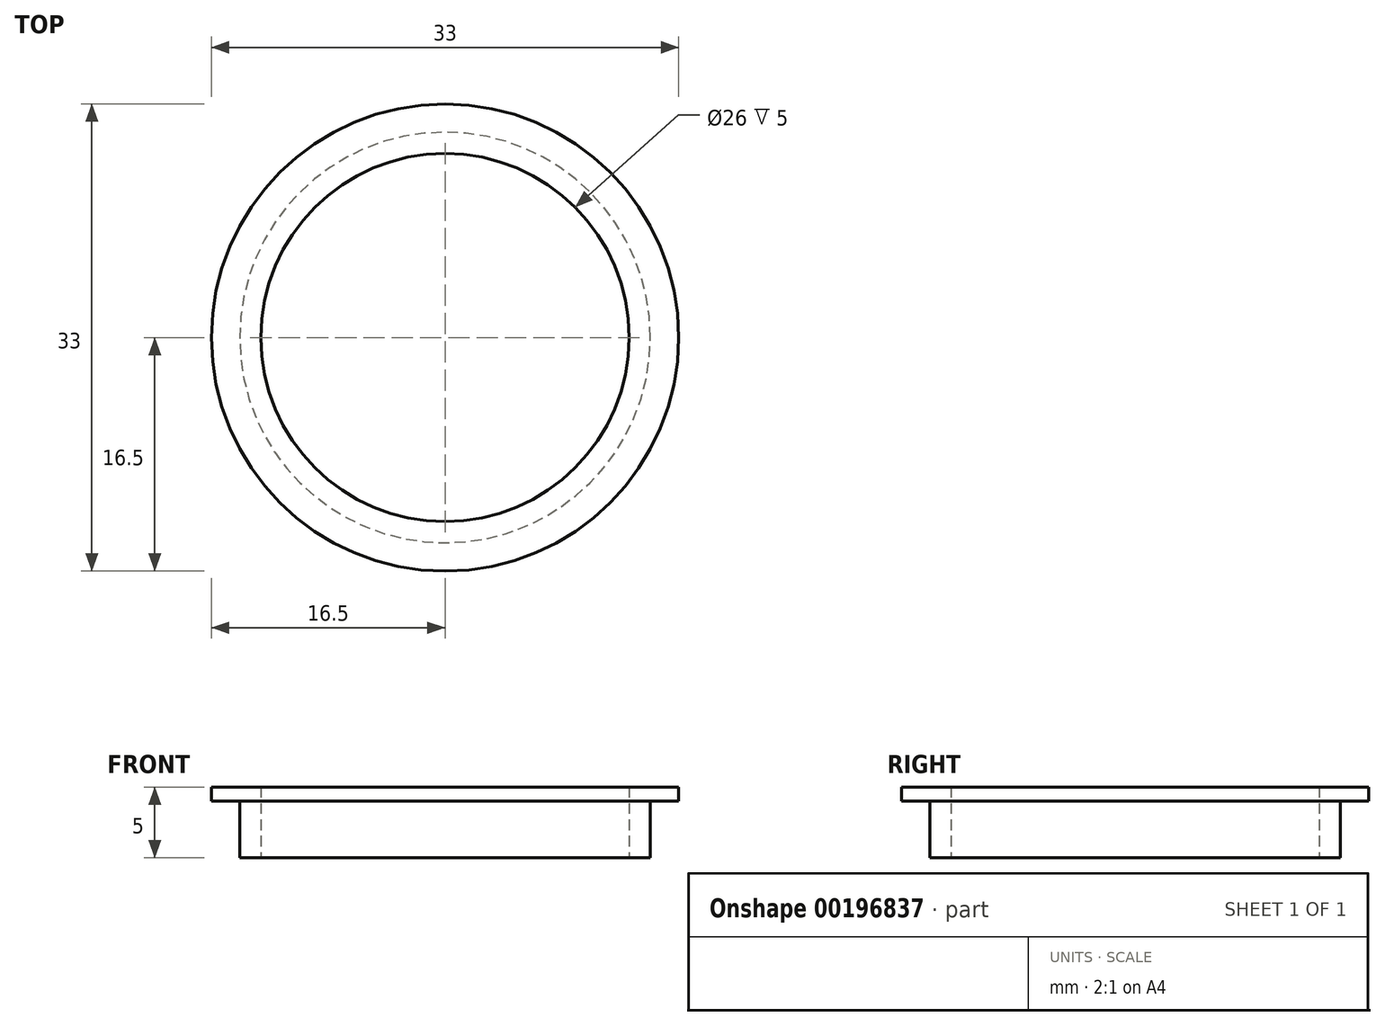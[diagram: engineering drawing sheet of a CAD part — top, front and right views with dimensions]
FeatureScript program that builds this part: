
annotation { "Feature Type Name" : "Feature", "Feature Type Description" : "" }
export const myFeature = defineFeature(function(context is Context, id is Id, definition is map)
    precondition{}
    {
        {
            var Q0;
            Q0=qCreatedBy(makeId("Top.planeOp"),FACE);
            var sketch = newSketch(context, id + "F0", { "sketchPlane" : qUnion([Q0])});
            skCircle(sketch, "E0", {"center": v(0, 0) * mm, "radius": 13 * mm});
            skCircle(sketch, "E1", {"center": v(0, 0) * mm, "radius": 14.5 * mm});
            skSolve(sketch);
        }
        {
            var Q0;
            Q0=qSketchRegion(id+"F0",true);
            extrude(context, id + "F1", {"entities" : qUnion([Q0]), "depth" : 5 * mm});
        }
        {
            var Q0;
            Q0=qCreatedBy(makeId("Front.planeOp"),FACE);
            var sketch = newSketch(context, id + "F2", { "sketchPlane" : qUnion([Q0])});
            skLineSegment(sketch, "E2", {"start": v(-14.5, 5) * mm, "end": v(-14.5, 4) * mm});
            skLineSegment(sketch, "E3", {"start": v(-16.5, 4) * mm, "end": v(-14.5, 4) * mm});
            skLineSegment(sketch, "E4", {"start": v(0, 0) * mm, "end": v(0, 34.69) * mm, "construction": true});
            skLineSegment(sketch, "E5", {"start": v(-14.5, 5) * mm, "end": v(-16.5, 5) * mm});
            skLineSegment(sketch, "E6", {"start": v(-16.5, 5) * mm, "end": v(-16.5, 4) * mm});
            skSolve(sketch);
        }
        {
            var Q0;
            Q0=qSketchRegion(id+"F2",true);
            var Q1;
            Q1=sQuery(id+"F2.wireOp",EDGE,"E4");
            revolve(context, id + "F3", {"operationType" : NewBodyOperationType.ADD, "entities" : qUnion([Q0]), "axis" : qUnion([Q1]), "revolveType" : RevolveType.FULL});
        }
    });
